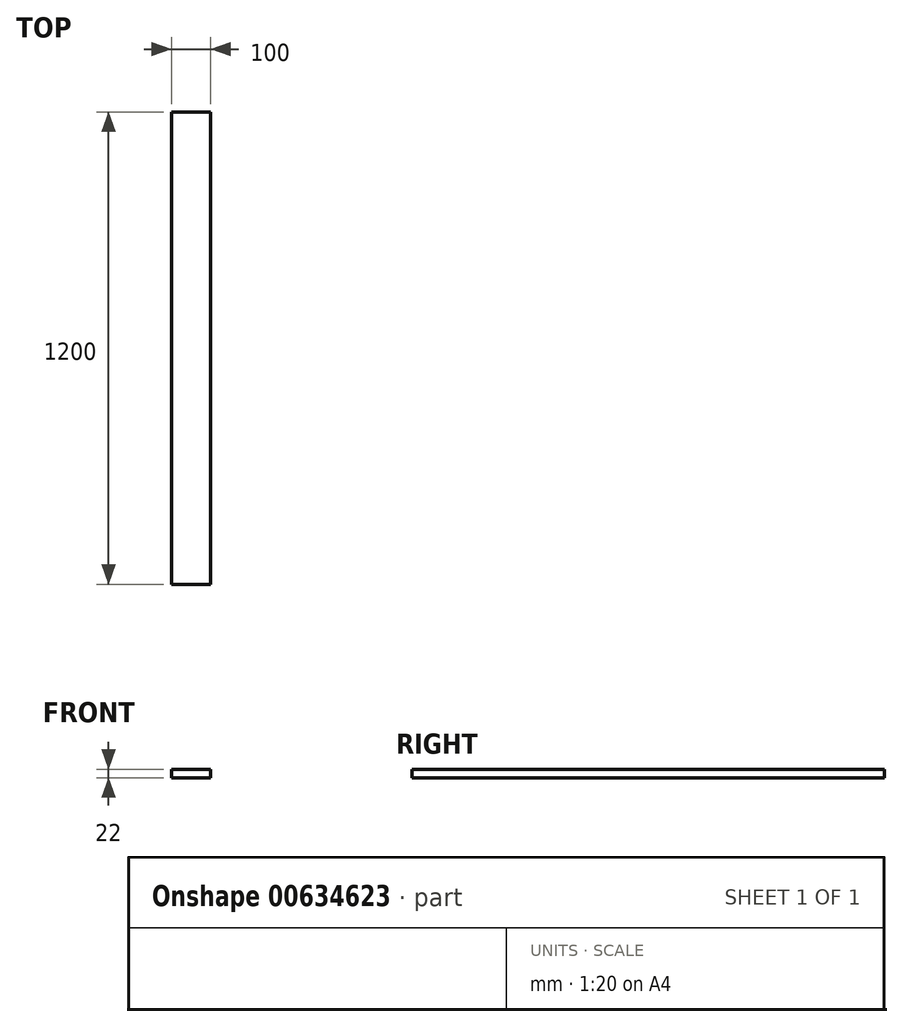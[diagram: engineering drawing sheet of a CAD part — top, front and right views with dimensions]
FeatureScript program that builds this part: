
annotation { "Feature Type Name" : "Feature", "Feature Type Description" : "" }
export const myFeature = defineFeature(function(context is Context, id is Id, definition is map)
    precondition{}
    {
        {
            var Q0;
            Q0=qCreatedBy(makeId("Top.planeOp"),FACE);
            var sketch = newSketch(context, id + "F0", { "sketchPlane" : qUnion([Q0])});
            skLineSegment(sketch, "E0.bottom", {"start": v(0, 0) * mm, "end": v(100, 0) * mm});
            skLineSegment(sketch, "E0.top", {"start": v(0, 1200) * mm, "end": v(100, 1200) * mm});
            skLineSegment(sketch, "E0.left", {"start": v(0, 0) * mm, "end": v(0, 1200) * mm});
            skLineSegment(sketch, "E0.right", {"start": v(100, 0) * mm, "end": v(100, 1200) * mm});
            skSolve(sketch);
        }
        {
            var Q0;
            Q0=makeQuery(id+"F0.imprint","IMPRINT",FACE,{"disambiguationData":[TD([[makeQuery(id+"F0.imprint","IMPRINT",EDGE,{"derivedFrom":sQuery(id+"F0.wireOp",EDGE,"E0.bottom")}),1.0]])]});
            extrude(context, id + "F1", {"entities" : qUnion([Q0]), "depth" : 22 * mm, "offsetDistance" : 25 * mm});
        }
    });
